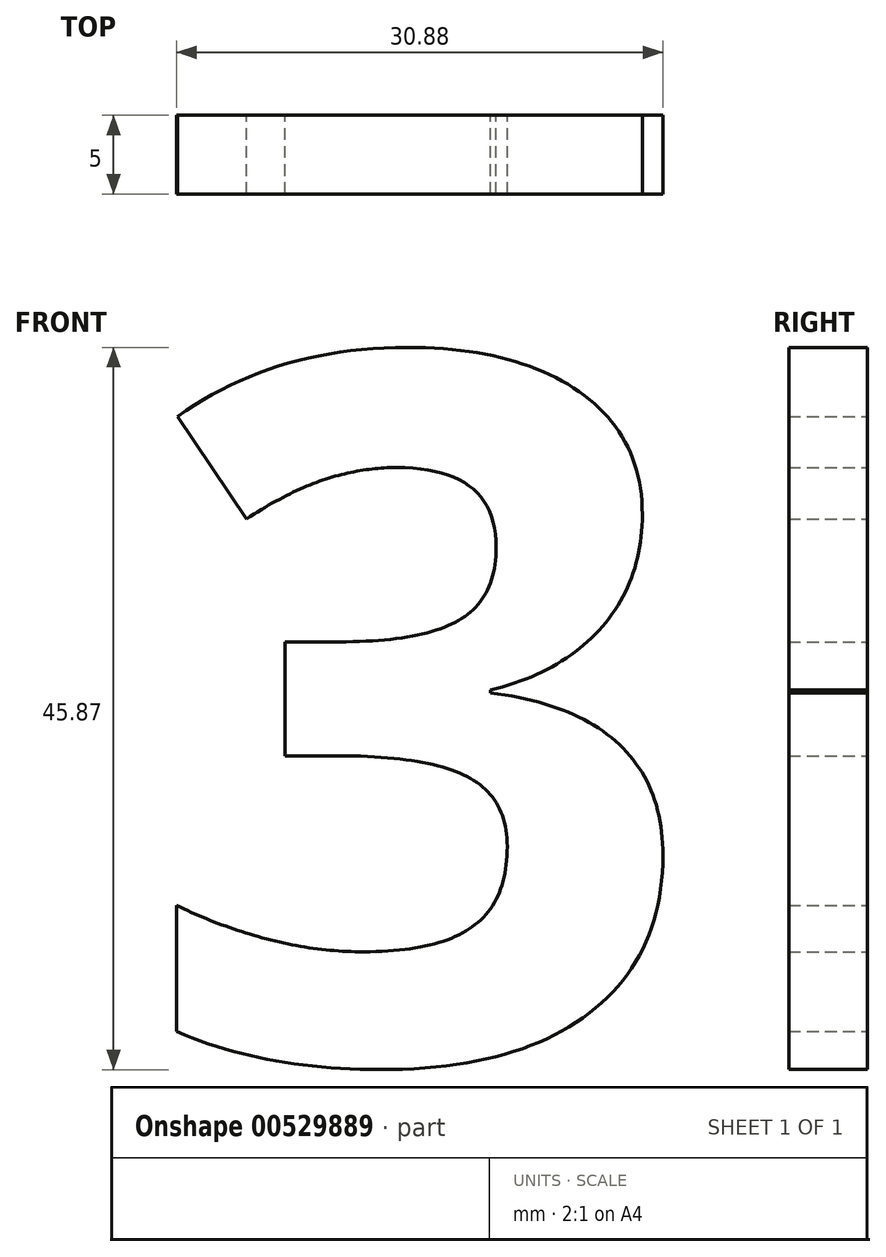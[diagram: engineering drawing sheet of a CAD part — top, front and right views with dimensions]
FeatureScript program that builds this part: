
annotation { "Feature Type Name" : "Feature", "Feature Type Description" : "" }
export const myFeature = defineFeature(function(context is Context, id is Id, definition is map)
    precondition{}
    {
        {
            var Q0;
            Q0=qCreatedBy(makeId("Front.planeOp"),FACE);
            var sketch = newSketch(context, id + "F0", { "sketchPlane" : qUnion([Q0])});
            skText(sketch, "E0", { "text": "3", "fontName": "OpenSans-Bold.ttf"});
            const initialGuessF0  = {"E0": [-0.05603, 0.01125, 1, 0, 0.045]};
            skSetInitialGuess(sketch, initialGuessF0);
            skSolve(sketch);
        }
        {
            var Q0;
            Q0=makeQuery(id+"F0.imprint","IMPRINT",FACE,{"disambiguationData":[TD([[makeQuery(id+"F0.imprint","IMPRINT",EDGE,{"derivedFrom":sQuery(id+"F0.wireOp",EDGE,"E0.sketch_text.stroke-0")}),-1.0]])]});
            extrude(context, id + "F1", {"entities" : qUnion([Q0]), "depth" : 5 * mm, "offsetDistance" : 25 * mm});
        }
    });
